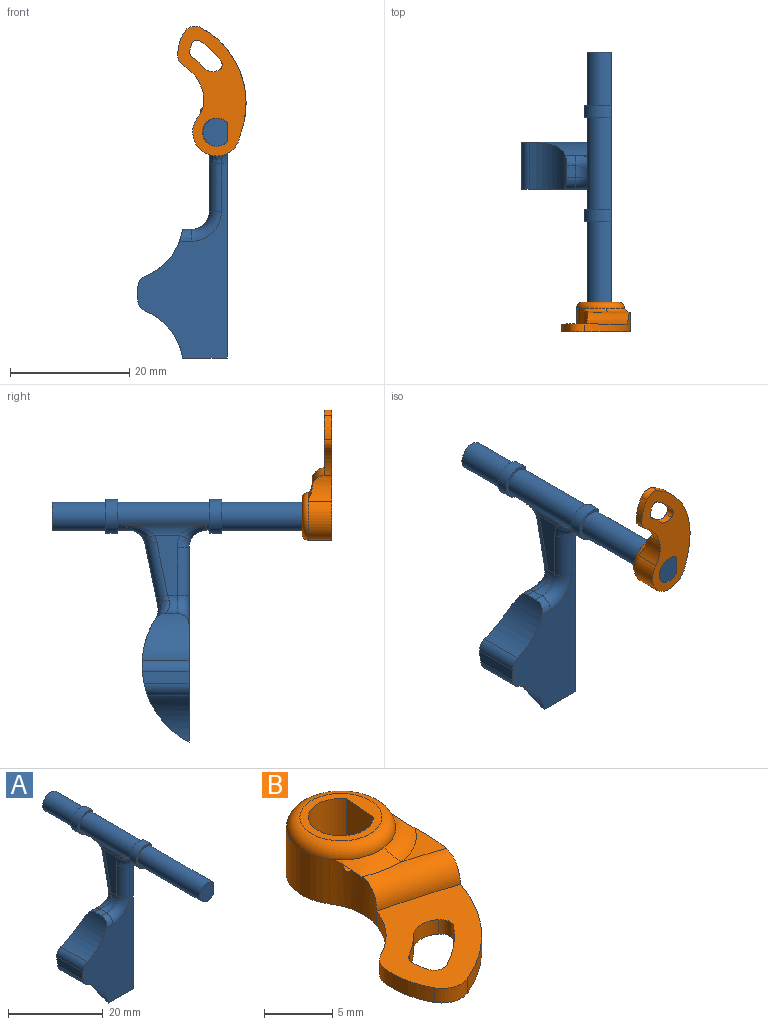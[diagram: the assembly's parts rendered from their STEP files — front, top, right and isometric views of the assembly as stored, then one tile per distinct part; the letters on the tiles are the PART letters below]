
ASSEMBLY  parts=2 mates=1
PART A: 38 faces, bbox 19.5x47.3x41.1 mm
  f0: cylinder r=2.35mm len=15.5mm, axis (0,1,0), area 118.3mm2, adj f7,f14,f18,f20,f21,f22
  f1: cylinder r=2.35mm len=9mm, axis (0,1,0), area 100.7mm2, adj f7,f9,f17
  f2: plane 1.95x1.5mm, normal (0,0,1), area 2.9mm2, adj f13,f24,f30,f31
  f3: cylinder r=14.52mm len=20.66mm, axis (1,0,0), area 257mm2, adj f4,f5,f7,f12,f13,f23,f36,f37
  f4: plane 32.85x15mm, normal (0,-1,0), area 238.8mm2, adj f3,f5,f7,f12,f13,f20,f31,f32
  f5: plane 7.85x2.12mm, normal (-1,0,0), area 16.4mm2, adj f3,f4,f36,f37
  f6: cylinder r=2.35mm len=18.5mm, axis (0,1,0), area 206.9mm2, adj f7,f8,f15
  f7: plane 47.35x40.56mm, normal (1,0,0), area 390.9mm2, adj f0,f1,f3,f4,f6,f8,f9,f11
  f8: plane 4.7x4.05mm, normal (0,-1,0), area 15.9mm2, adj f6,f7
  f9: plane 4.7x4.05mm, normal (0,1,0), area 15.9mm2, adj f1,f7
  f10: plane 10.13x4.24mm, normal (-1,0,0), area 26.8mm2, adj f21,f24,f26,f27,f33,f34
  f11: plane 10.59x2.16mm, normal (0,0.98,-0.2), area 10.8mm2, adj f7,f22,f23,f27,f28
  f12: cylinder r=10.19mm len=7.89mm, axis (0,-1,0), area 36.8mm2, adj f3,f4,f36
  f13: cylinder r=10.19mm len=7.89mm, axis (0,-1,0), area 73.1mm2, adj f2,f3,f4,f23,f30,f31,f37
  f14: plane 5.7x4.55mm, normal (0,1,0), area 5.9mm2, adj f0,f7,f16
  f15: plane 5.7x4.55mm, normal (0,-1,0), area 5.9mm2, adj f6,f7,f16
  f16: cylinder r=2.85mm len=5.7mm, axis (0,-1,0), area 25.2mm2, adj f7,f14,f15
  f17: plane 5.7x4.55mm, normal (0,1,0), area 5.9mm2, adj f1,f7,f19
  f18: plane 5.7x4.55mm, normal (0,-1,0), area 5.9mm2, adj f0,f7,f19
  f19: cylinder r=2.85mm len=5.7mm, axis (0,-1,0), area 25.2mm2, adj f7,f17,f18
  f20: torus R=5.35mm, axis (0,-1,0), area 6.8mm2, adj f0,f4,f7,f34,f35
  f21: cylinder r=3mm len=13.74mm, axis (0,1,0), area 17.2mm2, adj f0,f10,f25,f35
  f22: bspline ~8.17x3.39mm, area 6.7mm2, adj f0,f7,f11,f25,f26
  f23: cylinder r=3mm len=7.7mm, axis (1,0,0), area 5.8mm2, adj f3,f7,f11,f13,f29,f30
  f24: cylinder r=3mm len=3mm, axis (0,-1,0), area 7.5mm2, adj f2,f10,f28,f29,f32
  f25: bspline ~5.26x3.11mm, area 5.7mm2, adj f21,f22,f26
  f26: bspline ~3.3x2.86mm, area 2.8mm2, adj f10,f22,f25,f27
  f27: cylinder r=2mm len=9.41mm, axis (0,0.2,0.98), area 28.9mm2, adj f10,f11,f26,f28
  f28: bspline ~2.24x2.11mm, area 3.4mm2, adj f11,f24,f27,f29
  f29: bspline ~6.02x3.63mm, area 11.2mm2, adj f23,f24,f28,f30
  f30: cylinder r=2mm len=1.7mm, axis (1,0,0), area 3.2mm2, adj f2,f13,f23,f29
  f31: cylinder r=2mm len=2.02mm, axis (1,0,0), area 5.5mm2, adj f2,f4,f13,f32
  f32: torus R=5mm, axis (0,-1,0), area 18.4mm2, adj f4,f24,f31,f33
  f33: cylinder r=2mm len=8mm, axis (0,0,1), area 25.1mm2, adj f4,f10,f32,f34
  f34: bspline ~3.52x2.56mm, area 5.3mm2, adj f10,f20,f33,f35
  f35: bspline ~4.58x2.83mm, area 9.5mm2, adj f20,f21,f34
  f36: cylinder r=2mm len=7.54mm, axis (0,-1,0), area 17.2mm2, adj f3,f4,f5,f12
  f37: cylinder r=2mm len=7.87mm, axis (0,-1,0), area 18.6mm2, adj f3,f4,f5,f13
PART B: 26 faces, bbox 15.2x21.8x5.3 mm
  f0: cylinder r=4mm len=7.98mm, axis (0,0,-1), area 58mm2, adj f4,f14,f15,f16
  f1: cylinder r=2.38mm len=5mm, axis (0,0,-1), area 57.7mm2, adj f2,f3,f4
  f2: plane 5x3.09mm, normal (-1,0.09,0), area 15.5mm2, adj f1,f3,f4
  f3: plane 6x6mm, normal (0,0,1), area 11.8mm2, adj f1,f2,f14
  f4: plane 21.47x12.23mm, normal (0,0,-1), area 123.6mm2, adj f0,f1,f2,f5,f6,f7,f8,f9
  f5: cylinder r=14.41mm len=16.86mm, axis (0,0,-1), area 41.7mm2, adj f4,f12,f13,f15,f17,f22,f24
  f6: cylinder r=6.97mm len=4.23mm, axis (0,0,-1), area 5.7mm2, adj f4,f12,f22,f23
  f7: cylinder r=4.97mm len=1.32mm, axis (0,0,-1), area 1.7mm2, adj f4,f12,f18,f21
  f8: cylinder r=12.41mm len=3.75mm, axis (0,0,-1), area 6.3mm2, adj f4,f12,f18,f19
  f9: cylinder r=2.09mm len=2.51mm, axis (0,0,-1), area 3.5mm2, adj f4,f12,f19,f20
  f10: cylinder r=9.41mm len=2.08mm, axis (0,0,-1), area 3.4mm2, adj f4,f12,f20,f21
  f11: cylinder r=7.41mm len=4.07mm, axis (0,0,-1), area 7.3mm2, adj f4,f12,f16,f23
  f12: plane 11.52x10.88mm, normal (0,0,1), area 58.9mm2, adj f5,f6,f7,f8,f9,f10,f11,f17
  f13: plane 3.74x3.42mm, normal (0,0,1), area 5mm2, adj f5,f17,f24
  f14: torus R=3mm, axis (0,0,1), area 35.9mm2, adj f0,f3,f24,f25
  f15: cylinder r=5mm len=4mm, axis (0,0,1), area 3.2mm2, adj f0,f4,f5,f24
  f16: cylinder r=5mm len=4.43mm, axis (0,0,-1), area 14.3mm2, adj f0,f4,f11,f17,f25
  f17: torus R=61.88mm, axis (0,0,1), area 21.4mm2, adj f5,f12,f13,f16,f25
  f18: cylinder r=1mm len=1.43mm, axis (0,0,1), area 2.3mm2, adj f4,f7,f8,f12
  f19: cylinder r=1mm len=1.42mm, axis (0,0,1), area 2.1mm2, adj f4,f8,f9,f12
  f20: cylinder r=1mm len=1.3mm, axis (0,0,-1), area 0.2mm2, adj f4,f9,f10,f12
  f21: cylinder r=1mm len=1.3mm, axis (0,0,-1), area 1.4mm2, adj f4,f7,f10,f12
  f22: cylinder r=2mm len=2.52mm, axis (0,0,-1), area 3.8mm2, adj f4,f5,f6,f12
  f23: cylinder r=2mm len=1.56mm, axis (0,0,1), area 2.6mm2, adj f4,f6,f11,f12
  f24: torus R=5.52mm, axis (0,0,1), area 8.9mm2, adj f5,f13,f14,f15,f25
  f25: bspline ~6.68x3.69mm, area 6.7mm2, adj f14,f16,f17,f24
PLACE A at identity fixed
PLACE B rot(axis=(-1,0.04,0.04),90.1deg) t=(-0.1,-47,0)mm
MATE fastened B.f2 <-> A.f7  axis (-1,0,0) through (1.7,-47,0)mm
